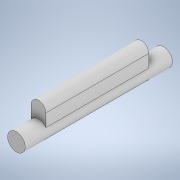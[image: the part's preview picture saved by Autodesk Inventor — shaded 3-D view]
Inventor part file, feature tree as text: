
AUTODESK INVENTOR PART (.ipt)
format: ipt  version: 2020 (Build 240168000, 168)  size: 125,440 bytes
history: native  units: mm
features: sketch x4, extrude x3
ambient origin geometry x8: Origin, YZ Plane, XZ Plane, XY Plane, X Axis, Y Axis, Z Axis, Center Point
bodies: Body1 (feature_tree)
feature tree (7):
  extrude  "Выдавливание3"  Depth=6.0mm
  extrude  "Выдавливание4"  Depth=50.0mm TaperAngle=0.0deg
  sketch  "Эскиз6"
  extrude  "Выдавливание5"  Depth=25.0mm
  sketch  "Эскиз4"
  sketch  "Эскиз5"
  sketch  "Эскиз7"
